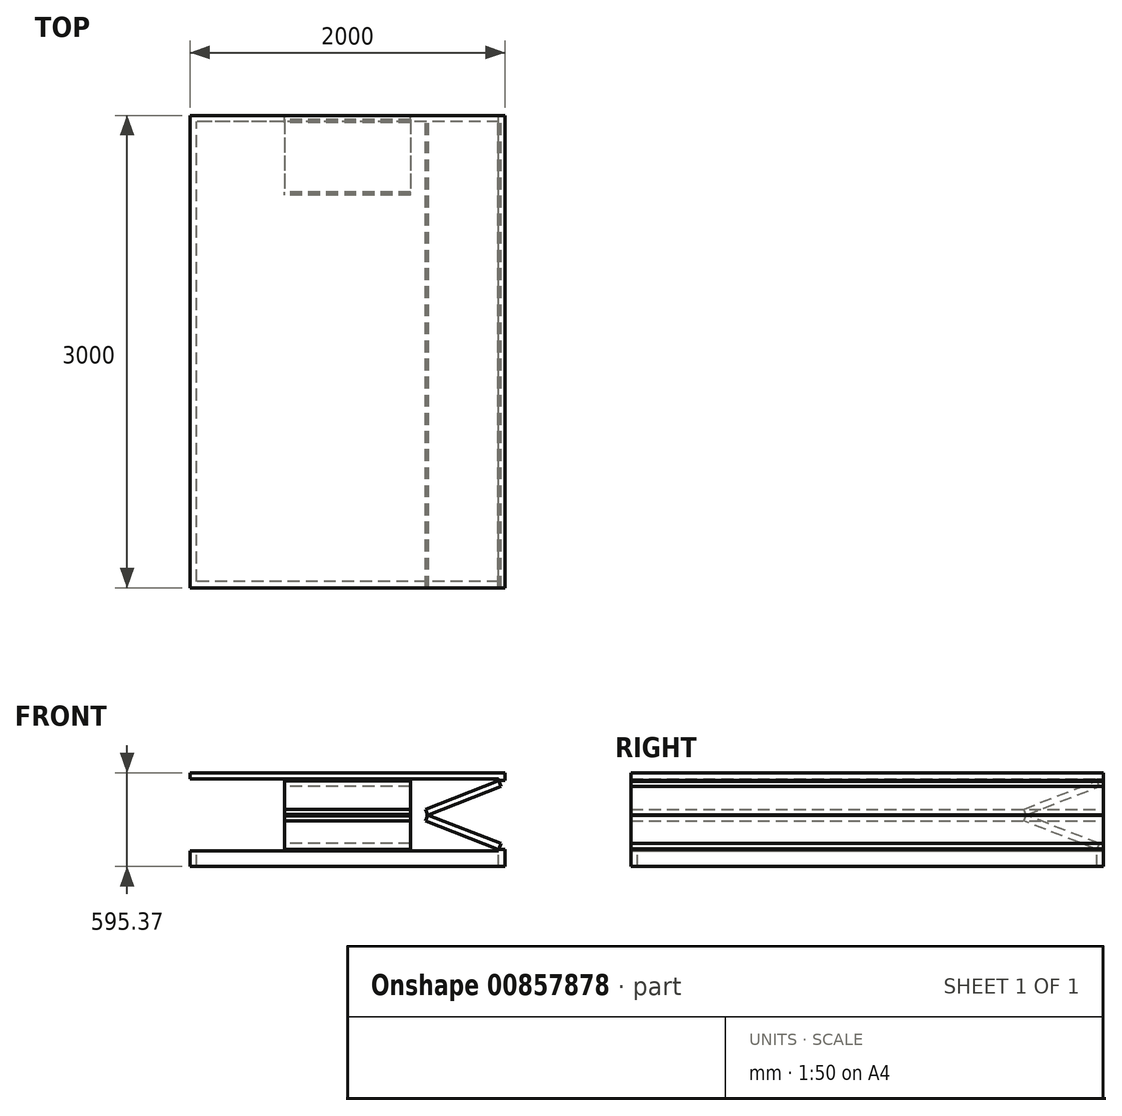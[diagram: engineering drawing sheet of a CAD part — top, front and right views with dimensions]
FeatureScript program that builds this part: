
annotation { "Feature Type Name" : "Feature", "Feature Type Description" : "" }
export const myFeature = defineFeature(function(context is Context, id is Id, definition is map)
    precondition{}
    {
        {
            var Q0;
            Q0=qCreatedBy(makeId("Front.planeOp"),FACE);
            var sketch = newSketch(context, id + "F0", { "sketchPlane" : qUnion([Q0])});
            skLineSegment(sketch, "E0.bottom", {"start": v(0, 0) * mm, "end": v(-465.93, 181.41) * mm});
            skLineSegment(sketch, "E0.top", {"start": v(14.51, 37.27) * mm, "end": v(-451.42, 218.68) * mm});
            skLineSegment(sketch, "E0.left", {"start": v(0, 0) * mm, "end": v(14.51, 37.27) * mm});
            skLineSegment(sketch, "E0.right", {"start": v(-465.93, 181.41) * mm, "end": v(-451.42, 218.68) * mm});
            skLineSegment(sketch, "E1.bottom", {"start": v(-451.42, 218.68) * mm, "end": v(14.51, 400.1) * mm});
            skLineSegment(sketch, "E1.top", {"start": v(-465.93, 255.96) * mm, "end": v(0, 437.37) * mm});
            skLineSegment(sketch, "E1.left", {"start": v(-451.42, 218.68) * mm, "end": v(-465.93, 255.96) * mm});
            skLineSegment(sketch, "E1.right", {"start": v(14.51, 400.1) * mm, "end": v(0, 437.37) * mm});
            skLineSegment(sketch, "E2.bottom", {"start": v(0, 0) * mm, "end": v(40, 0) * mm});
            skLineSegment(sketch, "E2.top", {"start": v(0, -10) * mm, "end": v(40, -10) * mm});
            skLineSegment(sketch, "E2.left", {"start": v(0, 0) * mm, "end": v(0, -10) * mm});
            skLineSegment(sketch, "E2.right", {"start": v(40, 0) * mm, "end": v(40, -10) * mm});
            skLineSegment(sketch, "E3.bottom", {"start": v(0, 437.37) * mm, "end": v(40, 437.37) * mm});
            skLineSegment(sketch, "E3.top", {"start": v(0, 447.37) * mm, "end": v(40, 447.37) * mm});
            skLineSegment(sketch, "E3.left", {"start": v(0, 437.37) * mm, "end": v(0, 447.37) * mm});
            skLineSegment(sketch, "E3.right", {"start": v(40, 437.37) * mm, "end": v(40, 447.37) * mm});
            skCircle(sketch, "E4", {"center": v(0, 437.37) * mm, "radius": 5 * mm});
            skCircle(sketch, "E5", {"center": v(-451.42, 218.68) * mm, "radius": 5 * mm});
            skCircle(sketch, "E6", {"center": v(0, 0) * mm, "radius": 5 * mm});
            skSolve(sketch);
        }
        {
            var Q0;
            {var subQ2=sQuery(id+"F0.wireOp",EDGE,"E3.top");Q0=makeQuery(id+"F0.imprint","IMPRINT",FACE,{"disambiguationData":[TD([[makeQuery(id+"F0.imprint","IMPRINT",EDGE,{"derivedFrom":subQ2}),-1.0]])]});}
            var Q1;
            {var subQ7=sQuery(id+"F0.wireOp",EDGE,"E1.bottom");var subQ9=sQuery(id+"F0.wireOp",EDGE,"E1.right");var subQ10=makeQuery(id+"F0.imprint","INTERSECT",VERTEX,{"derivedFrom":[subQ7,subQ9]});Q1=makeQuery(id+"F0.imprint","IMPRINT",FACE,{"disambiguationData":[TD([[makeQuery(id+"F0.imprint","IMPRINT",EDGE,{"disambiguationData":[TD([[subQ10,1.0]])],"derivedFrom":subQ7}),1.0]])]});}
            var Q2;
            {var subQ7=sQuery(id+"F0.wireOp",EDGE,"E0.right");var subQ8=sQuery(id+"F0.wireOp",EDGE,"E0.bottom");var subQ9=makeQuery(id+"F0.imprint","INTERSECT",VERTEX,{"derivedFrom":[subQ8,subQ7]});Q2=makeQuery(id+"F0.imprint","IMPRINT",FACE,{"disambiguationData":[TD([[makeQuery(id+"F0.imprint","IMPRINT",EDGE,{"disambiguationData":[TD([[subQ9,1.0]])],"derivedFrom":subQ8}),-1.0]])]});}
            var Q3;
            {var subQ2=sQuery(id+"F0.wireOp",EDGE,"E2.top");Q3=makeQuery(id+"F0.imprint","IMPRINT",FACE,{"disambiguationData":[TD([[makeQuery(id+"F0.imprint","IMPRINT",EDGE,{"derivedFrom":subQ2}),1.0]])]});}
            var Q4;
            {var subQ1=sQuery(id+"F0.wireOp",EDGE,"E2.bottom");var subQ3=sQuery(id+"F0.wireOp",EDGE,"E6");var subQ4=makeQuery(id+"F0.imprint","INTERSECT",VERTEX,{"derivedFrom":[subQ1,subQ3]});Q4=makeQuery(id+"F0.imprint","IMPRINT",FACE,{"disambiguationData":[TD([[makeQuery(id+"F0.imprint","IMPRINT",EDGE,{"disambiguationData":[TD([[subQ4,1.0]])],"derivedFrom":subQ3}),1.0]])]});}
            var Q5;
            {var subQ1=sQuery(id+"F0.wireOp",EDGE,"E0.left");var subQ3=sQuery(id+"F0.wireOp",EDGE,"E6");var subQ4=makeQuery(id+"F0.imprint","INTERSECT",VERTEX,{"derivedFrom":[subQ1,subQ3]});Q5=makeQuery(id+"F0.imprint","IMPRINT",FACE,{"disambiguationData":[TD([[makeQuery(id+"F0.imprint","IMPRINT",EDGE,{"disambiguationData":[TD([[subQ4,1.0]])],"derivedFrom":subQ3}),1.0]])]});}
            var Q6;
            {var subQ1=sQuery(id+"F0.wireOp",EDGE,"E0.bottom");var subQ3=sQuery(id+"F0.wireOp",EDGE,"E6");var subQ4=makeQuery(id+"F0.imprint","INTERSECT",VERTEX,{"derivedFrom":[subQ1,subQ3]});Q6=makeQuery(id+"F0.imprint","IMPRINT",FACE,{"disambiguationData":[TD([[makeQuery(id+"F0.imprint","IMPRINT",EDGE,{"disambiguationData":[TD([[subQ4,-1.0]])],"derivedFrom":subQ3}),1.0]])]});}
            var Q7;
            {var subQ1=sQuery(id+"F0.wireOp",EDGE,"E0.top");var subQ3=sQuery(id+"F0.wireOp",EDGE,"E5");var subQ4=makeQuery(id+"F0.imprint","INTERSECT",VERTEX,{"derivedFrom":[subQ1,subQ3]});Q7=makeQuery(id+"F0.imprint","IMPRINT",FACE,{"disambiguationData":[TD([[makeQuery(id+"F0.imprint","IMPRINT",EDGE,{"disambiguationData":[TD([[subQ4,1.0]])],"derivedFrom":subQ3}),1.0]])]});}
            var Q8;
            {var subQ1=sQuery(id+"F0.wireOp",EDGE,"E0.top");var subQ3=sQuery(id+"F0.wireOp",EDGE,"E5");var subQ4=makeQuery(id+"F0.imprint","INTERSECT",VERTEX,{"derivedFrom":[subQ1,subQ3]});Q8=makeQuery(id+"F0.imprint","IMPRINT",FACE,{"disambiguationData":[TD([[makeQuery(id+"F0.imprint","IMPRINT",EDGE,{"disambiguationData":[TD([[subQ4,-1.0]])],"derivedFrom":subQ3}),1.0]])]});}
            var Q9;
            {var subQ1=sQuery(id+"F0.wireOp",EDGE,"E0.right");var subQ3=sQuery(id+"F0.wireOp",EDGE,"E5");var subQ4=makeQuery(id+"F0.imprint","INTERSECT",VERTEX,{"derivedFrom":[subQ1,subQ3]});Q9=makeQuery(id+"F0.imprint","IMPRINT",FACE,{"disambiguationData":[TD([[makeQuery(id+"F0.imprint","IMPRINT",EDGE,{"disambiguationData":[TD([[subQ4,1.0]])],"derivedFrom":subQ3}),1.0]])]});}
            var Q10;
            {var subQ1=sQuery(id+"F0.wireOp",EDGE,"E1.right");var subQ3=sQuery(id+"F0.wireOp",EDGE,"E4");var subQ4=makeQuery(id+"F0.imprint","INTERSECT",VERTEX,{"derivedFrom":[subQ1,subQ3]});Q10=makeQuery(id+"F0.imprint","IMPRINT",FACE,{"disambiguationData":[TD([[makeQuery(id+"F0.imprint","IMPRINT",EDGE,{"disambiguationData":[TD([[subQ4,-1.0]])],"derivedFrom":subQ3}),1.0]])]});}
            var Q11;
            {var subQ1=sQuery(id+"F0.wireOp",EDGE,"E1.top");var subQ3=sQuery(id+"F0.wireOp",EDGE,"E4");var subQ4=makeQuery(id+"F0.imprint","INTERSECT",VERTEX,{"derivedFrom":[subQ1,subQ3]});Q11=makeQuery(id+"F0.imprint","IMPRINT",FACE,{"disambiguationData":[TD([[makeQuery(id+"F0.imprint","IMPRINT",EDGE,{"disambiguationData":[TD([[subQ4,-1.0]])],"derivedFrom":subQ3}),1.0]])]});}
            var Q12;
            {var subQ1=sQuery(id+"F0.wireOp",EDGE,"E1.top");var subQ3=sQuery(id+"F0.wireOp",EDGE,"E4");var subQ4=makeQuery(id+"F0.imprint","INTERSECT",VERTEX,{"derivedFrom":[subQ1,subQ3]});Q12=makeQuery(id+"F0.imprint","IMPRINT",FACE,{"disambiguationData":[TD([[makeQuery(id+"F0.imprint","IMPRINT",EDGE,{"disambiguationData":[TD([[subQ4,1.0]])],"derivedFrom":subQ3}),1.0]])]});}
            extrude(context, id + "F1", {"entities" : qUnion([Q0, Q1, Q2, Q3, Q4, Q5, Q6, Q7, Q8, Q9, Q10, Q11, Q12]), "endBound" : BoundingType.SYMMETRIC, "depth" : 3000 * mm, "offsetDistance" : 25 * mm});
        }
        {
            var Q0;
            Q0=makeQuery(id+"F1.opExtrude","SWEPT_FACE",FACE,{"disambiguationData":[OSD([sQuery(id+"F0.wireOp",EDGE,"E3.top")])]});
            var sketch = newSketch(context, id + "F2", { "sketchPlane" : qUnion([Q0])});
            skLineSegment(sketch, "E7.bottom", {"start": v(40, 1500) * mm, "end": v(-1960, 1500) * mm});
            skLineSegment(sketch, "E7.top", {"start": v(40, -1500) * mm, "end": v(-1960, -1500) * mm});
            skLineSegment(sketch, "E7.left", {"start": v(40, 1500) * mm, "end": v(40, -1500) * mm});
            skLineSegment(sketch, "E7.right", {"start": v(-1960, 1500) * mm, "end": v(-1960, -1500) * mm});
            skLineSegment(sketch, "E8.0", {"start": v(-1920, 1460) * mm, "end": v(-1920, -1460) * mm});
            skLineSegment(sketch, "E8.1", {"start": v(0, 1460) * mm, "end": v(-1920, 1460) * mm});
            skLineSegment(sketch, "E8.2", {"start": v(0, 1460) * mm, "end": v(0, -1460) * mm});
            skLineSegment(sketch, "E8.3", {"start": v(0, -1460) * mm, "end": v(-1920, -1460) * mm});
            skSolve(sketch);
        }
        {
            var Q0;
            {var subQ2=sQuery(id+"F2.wireOp",EDGE,"E7.right");Q0=makeQuery(id+"F2.imprint","IMPRINT",FACE,{"disambiguationData":[TD([[makeQuery(id+"F2.imprint","IMPRINT",EDGE,{"derivedFrom":subQ2}),1.0]])]});}
            var Q1;
            {var subQ2=sQuery(id+"F2.wireOp",EDGE,"E7.left");Q1=makeQuery(id+"F2.imprint","IMPRINT",FACE,{"disambiguationData":[TD([[makeQuery(id+"F2.imprint","IMPRINT",EDGE,{"derivedFrom":subQ2}),1.0]])]});}
            var Q2;
            Q2=makeQuery(id+"F2.imprint","IMPRINT",FACE,{"disambiguationData":[TD([[makeQuery(id+"F2.imprint","IMPRINT",EDGE,{"derivedFrom":sQuery(id+"F2.wireOp",EDGE,"E8.0")}),1.0]])]});
            extrude(context, id + "F3", {"entities" : qUnion([Q0, Q1, Q2]), "operationType" : NewBodyOperationType.ADD, "depth" : 40 * mm, "offsetDistance" : 25 * mm});
        }
        {
            var Q0;
            Q0=makeQuery(id+"F1.opExtrude","SWEPT_FACE",FACE,{"disambiguationData":[OSD([sQuery(id+"F0.wireOp",EDGE,"E2.top")])]});
            var sketch = newSketch(context, id + "F4", { "sketchPlane" : qUnion([Q0])});
            skLineSegment(sketch, "E9.bottom", {"start": v(40, 1500) * mm, "end": v(-1960, 1500) * mm});
            skLineSegment(sketch, "E9.top", {"start": v(40, -1500) * mm, "end": v(-1960, -1500) * mm});
            skLineSegment(sketch, "E9.left", {"start": v(40, 1500) * mm, "end": v(40, -1500) * mm});
            skLineSegment(sketch, "E9.right", {"start": v(-1960, 1500) * mm, "end": v(-1960, -1500) * mm});
            skLineSegment(sketch, "E10.0", {"start": v(0, 1460) * mm, "end": v(-1920, 1460) * mm});
            skLineSegment(sketch, "E10.1", {"start": v(0, 1460) * mm, "end": v(0, -1460) * mm});
            skLineSegment(sketch, "E10.2", {"start": v(0, -1460) * mm, "end": v(-1920, -1460) * mm});
            skLineSegment(sketch, "E10.3", {"start": v(-1920, 1460) * mm, "end": v(-1920, -1460) * mm});
            skSolve(sketch);
        }
        {
            var Q0;
            {var subQ4=sQuery(id+"F4.wireOp",EDGE,"E9.right");Q0=makeQuery(id+"F4.imprint","IMPRINT",FACE,{"disambiguationData":[TD([[makeQuery(id+"F4.imprint","IMPRINT",EDGE,{"derivedFrom":subQ4}),1.0]])]});}
            var Q1;
            {var subQ1=sQuery(id+"F4.wireOp",EDGE,"E9.left");Q1=makeQuery(id+"F4.imprint","IMPRINT",FACE,{"disambiguationData":[TD([[makeQuery(id+"F4.imprint","IMPRINT",EDGE,{"derivedFrom":subQ1}),-1.0]])]});}
            extrude(context, id + "F5", {"entities" : qUnion([Q0, Q1]), "operationType" : NewBodyOperationType.ADD, "depth" : 98 * mm, "offsetDistance" : 25 * mm});
        }
        {
            var Q0;
            Q0=makeQuery(id+"F3.opExtrude","CAP_EDGE",EDGE,{"disambiguationData":[OSD([sQuery(id+"F2.wireOp",EDGE,"E7.bottom")])],"isStart":false});
            cPoint(context, id + "F6", {"entities" : qUnion([Q0]), "parameter" : 0.5});
        }
        {
            var Q0;
            Q0 = qCreatedBy(id + "F6" ,VERTEX);
            var Q1;
            Q1=qCreatedBy(makeId("Right.planeOp"),FACE);
            cPlane(context, id + "F7", {"entities" : qUnion([Q0, Q1]), "cplaneType" : CPlaneType.PLANE_POINT, "offset" : 25 * mm, "width" : 150 * mm, "height" : 150 * mm});
        }
        {
            var Q0;
            Q0=qCreatedBy(id+"F7.planeOp",FACE);
            var sketch = newSketch(context, id + "F8", { "sketchPlane" : qUnion([Q0])});
            skLineSegment(sketch, "E11.bottom", {"start": v(1460, 0) * mm, "end": v(994.07, 181.41) * mm});
            skLineSegment(sketch, "E11.top", {"start": v(1474.51, 37.27) * mm, "end": v(1008.58, 218.68) * mm});
            skLineSegment(sketch, "E11.left", {"start": v(1460, 0) * mm, "end": v(1474.51, 37.27) * mm});
            skLineSegment(sketch, "E11.right", {"start": v(994.07, 181.41) * mm, "end": v(1008.58, 218.68) * mm});
            skLineSegment(sketch, "E12.bottom", {"start": v(1008.58, 218.68) * mm, "end": v(1474.51, 400.1) * mm});
            skLineSegment(sketch, "E12.top", {"start": v(994.07, 255.96) * mm, "end": v(1460, 437.37) * mm});
            skLineSegment(sketch, "E12.left", {"start": v(1008.58, 218.68) * mm, "end": v(994.07, 255.96) * mm});
            skLineSegment(sketch, "E12.right", {"start": v(1474.51, 400.1) * mm, "end": v(1460, 437.37) * mm});
            skLineSegment(sketch, "E13.bottom", {"start": v(1460, 0) * mm, "end": v(1500, 0) * mm});
            skLineSegment(sketch, "E13.top", {"start": v(1460, -10) * mm, "end": v(1500, -10) * mm});
            skLineSegment(sketch, "E13.left", {"start": v(1460, 0) * mm, "end": v(1460, -10) * mm});
            skLineSegment(sketch, "E13.right", {"start": v(1500, 0) * mm, "end": v(1500, -10) * mm});
            skLineSegment(sketch, "E14.bottom", {"start": v(1460, 437.37) * mm, "end": v(1500, 437.37) * mm});
            skLineSegment(sketch, "E14.top", {"start": v(1460, 447.37) * mm, "end": v(1500, 447.37) * mm});
            skLineSegment(sketch, "E14.left", {"start": v(1460, 437.37) * mm, "end": v(1460, 447.37) * mm});
            skLineSegment(sketch, "E14.right", {"start": v(1500, 437.37) * mm, "end": v(1500, 447.37) * mm});
            skCircle(sketch, "E15", {"center": v(1460, 437.37) * mm, "radius": 5 * mm});
            skCircle(sketch, "E16", {"center": v(1008.58, 218.68) * mm, "radius": 5 * mm});
            skCircle(sketch, "E17", {"center": v(1460, 0) * mm, "radius": 5 * mm});
            skSolve(sketch);
        }
        {
            var Q0;
            {var subQ7=sQuery(id+"F8.wireOp",EDGE,"E12.bottom");var subQ9=sQuery(id+"F8.wireOp",EDGE,"E12.right");var subQ10=makeQuery(id+"F8.imprint","INTERSECT",VERTEX,{"derivedFrom":[subQ7,subQ9]});Q0=makeQuery(id+"F8.imprint","IMPRINT",FACE,{"disambiguationData":[TD([[makeQuery(id+"F8.imprint","IMPRINT",EDGE,{"disambiguationData":[TD([[subQ10,1.0]])],"derivedFrom":subQ7}),1.0]])]});}
            var Q1;
            {var subQ7=sQuery(id+"F8.wireOp",EDGE,"E11.right");var subQ8=sQuery(id+"F8.wireOp",EDGE,"E11.bottom");var subQ9=makeQuery(id+"F8.imprint","INTERSECT",VERTEX,{"derivedFrom":[subQ8,subQ7]});Q1=makeQuery(id+"F8.imprint","IMPRINT",FACE,{"disambiguationData":[TD([[makeQuery(id+"F8.imprint","IMPRINT",EDGE,{"disambiguationData":[TD([[subQ9,1.0]])],"derivedFrom":subQ8}),-1.0]])]});}
            var Q2;
            {var subQ2=sQuery(id+"F8.wireOp",EDGE,"E14.top");Q2=makeQuery(id+"F8.imprint","IMPRINT",FACE,{"disambiguationData":[TD([[makeQuery(id+"F8.imprint","IMPRINT",EDGE,{"derivedFrom":subQ2}),-1.0]])]});}
            var Q3;
            {var subQ1=sQuery(id+"F8.wireOp",EDGE,"E14.bottom");var subQ3=sQuery(id+"F8.wireOp",EDGE,"E15");var subQ4=makeQuery(id+"F8.imprint","INTERSECT",VERTEX,{"derivedFrom":[subQ1,subQ3]});Q3=makeQuery(id+"F8.imprint","IMPRINT",FACE,{"disambiguationData":[TD([[makeQuery(id+"F8.imprint","IMPRINT",EDGE,{"disambiguationData":[TD([[subQ4,-1.0]])],"derivedFrom":subQ3}),1.0]])]});}
            var Q4;
            {var subQ1=sQuery(id+"F8.wireOp",EDGE,"E12.top");var subQ3=sQuery(id+"F8.wireOp",EDGE,"E15");var subQ4=makeQuery(id+"F8.imprint","INTERSECT",VERTEX,{"derivedFrom":[subQ1,subQ3]});Q4=makeQuery(id+"F8.imprint","IMPRINT",FACE,{"disambiguationData":[TD([[makeQuery(id+"F8.imprint","IMPRINT",EDGE,{"disambiguationData":[TD([[subQ4,1.0]])],"derivedFrom":subQ3}),1.0]])]});}
            var Q5;
            {var subQ2=sQuery(id+"F8.wireOp",EDGE,"E13.top");Q5=makeQuery(id+"F8.imprint","IMPRINT",FACE,{"disambiguationData":[TD([[makeQuery(id+"F8.imprint","IMPRINT",EDGE,{"derivedFrom":subQ2}),1.0]])]});}
            extrude(context, id + "F9", {"entities" : qUnion([Q0, Q1, Q2, Q3, Q4, Q5]), "operationType" : NewBodyOperationType.ADD, "endBound" : BoundingType.SYMMETRIC, "depth" : 800 * mm, "offsetDistance" : 25 * mm});
        }
    });
